FCSTD DOCUMENT  (FreeCAD 1.0R39109 (Git))
Label: vsn_display_interface_new_freecad
License: All rights reserved
LicenseURL: https://en.wikipedia.org/wiki/All_rights_reserved
objects: App::Link×2, App::FeaturePython×2, Assembly::JointGroup×1, Assembly::AssemblyObject×1
EXTERNAL_REF file=vsn_display_interface.FCStd obj=b_VSN1_layer3_001_
EXTERNAL_REF file=../Design/PLASTIC-VSN-DISPLAY-SPACER/PLASTIC-VSN-DISPLAY-SPACER_1.FCStd obj=Body

FEATURE [App::Link] VSN1_layer3_001
  LinkedObject = -> <external vsn_display_interface.FCStd>#b_VSN1_layer3_001_
FEATURE [App::FeaturePython] GroundedJoint  # Assembly grounded joint (typed FeaturePython)
  ObjectToGround = -> VSN1_layer3_001
FEATURE [App::Link] Body
  LinkPlacement = pos=(-23.54,26.67,1.2) rot=(0,0,1;0rad)
  LinkedObject = -> <external ../Design/PLASTIC-VSN-DISPLAY-SPACER/PLASTIC-VSN-DISPLAY-SPACER_1.FCStd>#Body
  Placement = pos=(-23.54,26.67,1.2) rot=(0,0,1;0rad)
FEATURE [App::FeaturePython] Joint  label="Fixed"  # Assembly joint (typed FeaturePython)
  Activated = true
  AngleMax = 0
  AngleMin = 0
  Detach1 = false
  Detach2 = false
  Distance = 0
  Distance2 = 0
  EnableAngleMax = false
  EnableAngleMin = false
  EnableLengthMax = false
  EnableLengthMin = false
  JointType = 0 (Fixed)
  LengthMax = 0
  LengthMin = 0
  Offset2 = pos=(0,0,0) rot=(0,0,1;3.14159rad)
  Placement1 = pos=(-10.75,0,0) rot=(-0.57735,-0.57735,0.57735;4.18879rad)
  Placement2 = pos=(-34.29,26.67,1.2) rot=(0.57735,-0.57735,-0.57735;4.18879rad)
  Reference1 = -> Assembly [Body.Pad.Edge1,Body.Pad.Edge1]
  Reference2 = -> Assembly [VSN1_layer3_001.Edge1804,VSN1_layer3_001.Edge1804]
FEATURE [Assembly::JointGroup] Joints
  Group = -> [GroundedJoint,Joint]
FEATURE [Assembly::AssemblyObject] Assembly
  Group = -> [Joints,VSN1_layer3_001,GroundedJoint,Body,Joint]
  Origin = -> Origin
  Type = Assembly
